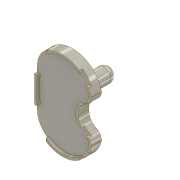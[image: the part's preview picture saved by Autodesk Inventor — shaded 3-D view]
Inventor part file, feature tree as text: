
AUTODESK INVENTOR PART (.ipt)
format: ipt  version: 2017 (Build 210142000, 142)  size: 226,816 bytes
history: native  units: mm
features: sketch x4, extrude x3, other x2, loft x1, fillet x1, projected_geometry x1
ambient origin geometry x8: Origin, YZ Plane, XZ Plane, XY Plane, X Axis, Y Axis, Z Axis, Center Point
bodies: Body1 (feature_tree)
feature tree (12):
  other  "Bryła1"
  sketch  "Szkic1"
  extrude  "Wyciągnięcie proste1"  Depth=15.0mm
  extrude  "Wyciągnięcie proste2"  Depth=30.0mm
  sketch  "Szkic5"
  other  "Płaszczyzna konstrukcyjna1"
  loft  "Wyciągnięcie złożone1"
  extrude  "Wyciągnięcie proste3"  Depth=20.0mm
  fillet  "Zaokrąglenie1"  Radius=38.5mm
  projected_geometry  "Pętla rzutowana1"
  sketch  "Szkic6"
  sketch  "Szkic7"
